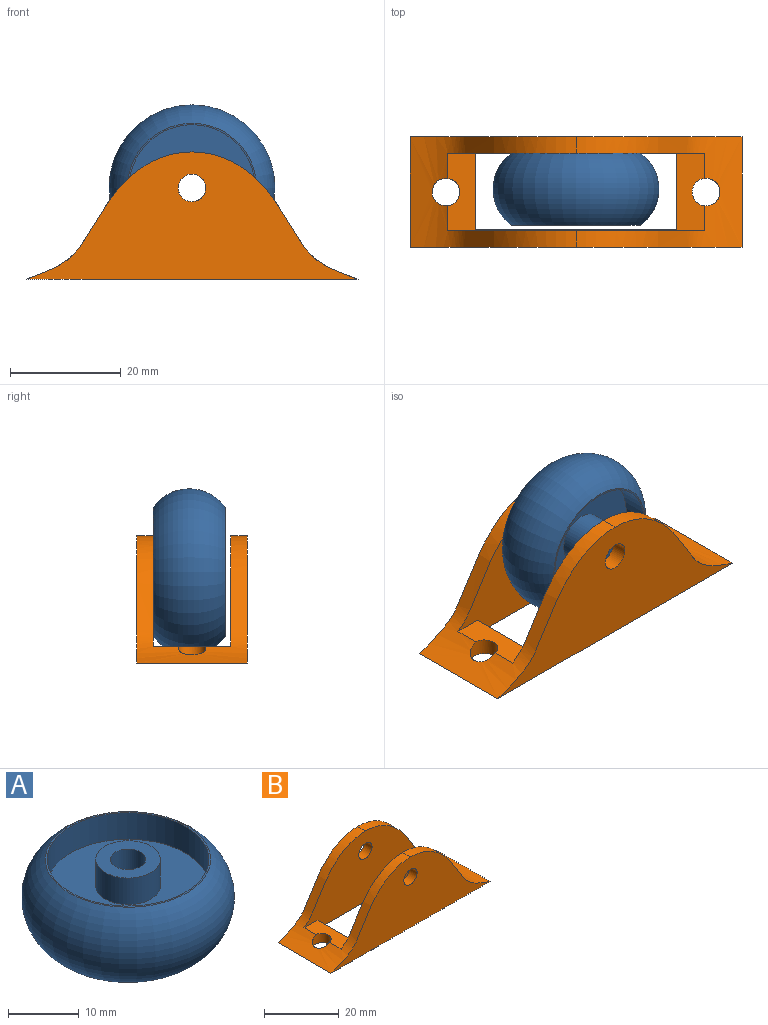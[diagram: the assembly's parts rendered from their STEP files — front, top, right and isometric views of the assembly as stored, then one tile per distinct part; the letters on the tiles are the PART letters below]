
ASSEMBLY  parts=2 mates=1
PART A: 12 faces, bbox 30x30x13 mm
  f0: cylinder r=2.5mm len=13mm, axis (0,0,-1), area 204.2mm2, adj f1,f11
  f1: plane 9.13x9.13mm, normal (0,0,1), area 45.8mm2, adj f0,f2
  f2: cylinder r=4.56mm len=9.13mm, axis (0,0,-1), area 131.4mm2, adj f1,f3
  f3: plane 22.81x22.81mm, normal (0,0,1), area 343.2mm2, adj f2,f4
  f4: cylinder r=11.4mm len=22.81mm, axis (0,0,-1), area 328.5mm2, adj f3,f5
  f5: plane 23.33x23.33mm, normal (0,0,1), area 18.8mm2, adj f4,f6
  f6: torus R=7mm, axis (0,0,-1), area 1320.9mm2, adj f5,f7
  f7: plane 23.33x23.33mm, normal (0,0,-1), area 18.8mm2, adj f6,f8
  f8: cylinder r=11.4mm len=22.81mm, axis (0,0,-1), area 328.5mm2, adj f7,f9
  f9: plane 22.81x22.81mm, normal (0,0,-1), area 343.2mm2, adj f8,f10
  f10: cylinder r=4.56mm len=9.13mm, axis (0,0,-1), area 131.4mm2, adj f9,f11
  f11: plane 9.13x9.13mm, normal (0,0,-1), area 45.8mm2, adj f0,f10
PART B: 15 faces, bbox 60x20x23 mm
  f0: plane 60x20mm, normal (0,0,-1), area 661.9mm2, adj f2,f4,f6,f7,f9,f10,f11,f12
  f1: plane 46.38x14mm, normal (0,0,1), area 134mm2, adj f2,f4,f8,f9,f10,f11,f12,f13
  f2: extruded ~30x23mm, area 328.6mm2, adj f0,f1,f4,f6,f7,f8,f9,f10
  f3: cylinder r=2.5mm len=5mm, axis (0,-1,0), area 47.1mm2, adj f6,f9
  f4: extruded ~30x23mm, area 328.6mm2, adj f0,f1,f2,f6,f7,f8,f9,f11
  f5: cylinder r=2.5mm len=5mm, axis (0,-1,0), area 47.1mm2, adj f7,f8
  f6: plane 60x23mm, normal (0,1,0), area 736.8mm2, adj f0,f2,f3,f4
  f7: plane 60x23mm, normal (0,-1,0), area 736.8mm2, adj f0,f2,f4,f5
  f8: plane 48.2x20.91mm, normal (0,1,0), area 579.7mm2, adj f1,f2,f4,f5
  f9: plane 48.2x23mm, normal (0,-1,0), area 688.8mm2, adj f0,f1,f2,f3,f4,f12,f14
  f10: cylinder r=2.5mm len=5mm, axis (0,0,-1), area 38.7mm2, adj f0,f1,f2
  f11: cylinder r=2.5mm len=5mm, axis (0,0,-1), area 38.7mm2, adj f0,f1,f4
  f12: plane 13.71x3mm, normal (1,0,0), area 41.1mm2, adj f0,f1,f9,f13
  f13: plane 36.38x3mm, normal (0,1,0), area 109.1mm2, adj f0,f1,f12,f14
  f14: plane 13.71x3mm, normal (-1,0,0), area 41.1mm2, adj f0,f1,f9,f13
PLACE A rot(axis=(1,0,0),90deg) t=(-13.6,2.96,9.87)mm
PLACE B t=(-13.6,-14.61,-6.63)mm fixed
MATE fastened B.f3 <-> A.f0  axis (0,-1,0) through (-13.6,2.39,9.87)mm
